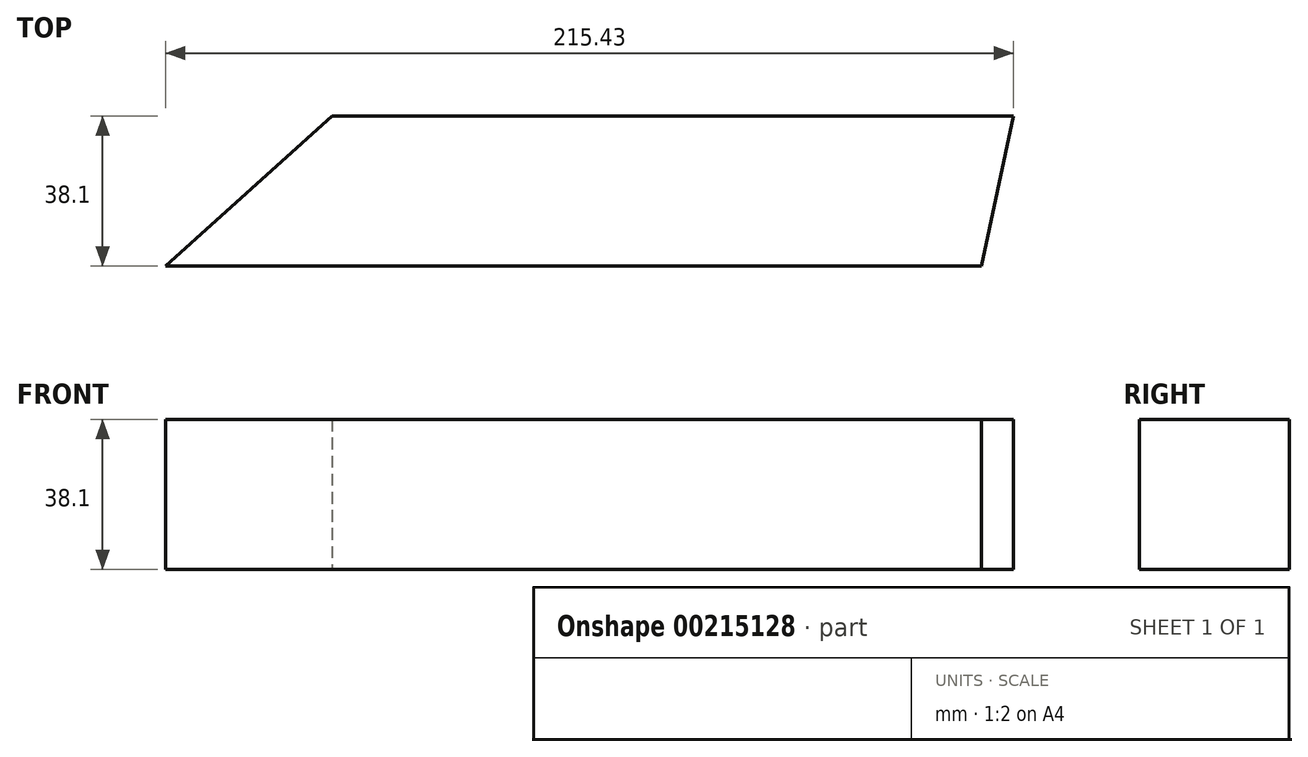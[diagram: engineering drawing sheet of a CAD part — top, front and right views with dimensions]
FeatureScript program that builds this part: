
annotation { "Feature Type Name" : "Feature", "Feature Type Description" : "" }
export const myFeature = defineFeature(function(context is Context, id is Id, definition is map)
    precondition{}
    {
        {
            var Q0;
            Q0=qCreatedBy(makeId("Top.planeOp"),FACE);
            var sketch = newSketch(context, id + "F0", { "sketchPlane" : qUnion([Q0])});
            skLineSegment(sketch, "E0", {"start": v(0, 0) * mm, "end": v(207.33, 0) * mm});
            skLineSegment(sketch, "E1", {"start": v(207.33, 0) * mm, "end": v(215.43, 38.1) * mm});
            skLineSegment(sketch, "E2", {"start": v(215.43, 38.1) * mm, "end": v(42.31, 38.1) * mm});
            skLineSegment(sketch, "E3", {"start": v(42.31, 38.1) * mm, "end": v(0, 0) * mm});
            skSolve(sketch);
        }
        {
            var Q0;
            Q0=makeQuery(id+"F0.imprint","IMPRINT",FACE,{"disambiguationData":[TD([[makeQuery(id+"F0.imprint","IMPRINT",EDGE,{"derivedFrom":sQuery(id+"F0.wireOp",EDGE,"E0")}),1.0]])]});
            extrude(context, id + "F1", {"entities" : qUnion([Q0]), "depth" : 38.1 * mm, "offsetDistance" : 25.4 * mm});
        }
    });
